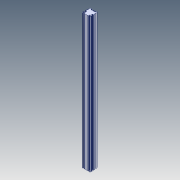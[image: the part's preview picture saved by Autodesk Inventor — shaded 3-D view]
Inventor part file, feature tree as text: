
AUTODESK INVENTOR PART (.ipt)
format: ipt  version: 2020 (Build 240168000, 168)  size: 384,512 bytes
history: native  units: mm
features: other x4, projected_geometry x3, extrude x2, sketch x2
ambient origin geometry x8: Origin, YZ Plane, XZ Plane, XY Plane, X Axis, Y Axis, Z Axis, Center Point
bodies: Body1 (feature_tree), Body2 (feature_tree)
feature tree (11):
  other  "ソリッド1"
  extrude  "押し出し1"  Depth=672.0mm TaperAngle=0.0deg
  extrude  "押し出し2"  Depth=672.0mm TaperAngle=0.0deg
  other  "ソリッド2"
  sketch  "スケッチ1"
  projected_geometry  "投影ループ1"
  projected_geometry  "投影ループ2"
  sketch  "スケッチ2"
  projected_geometry  "投影ループ3"
  other  "Boss-Extrude1[1]"
  other  "Boss-Extrude1[2]"
